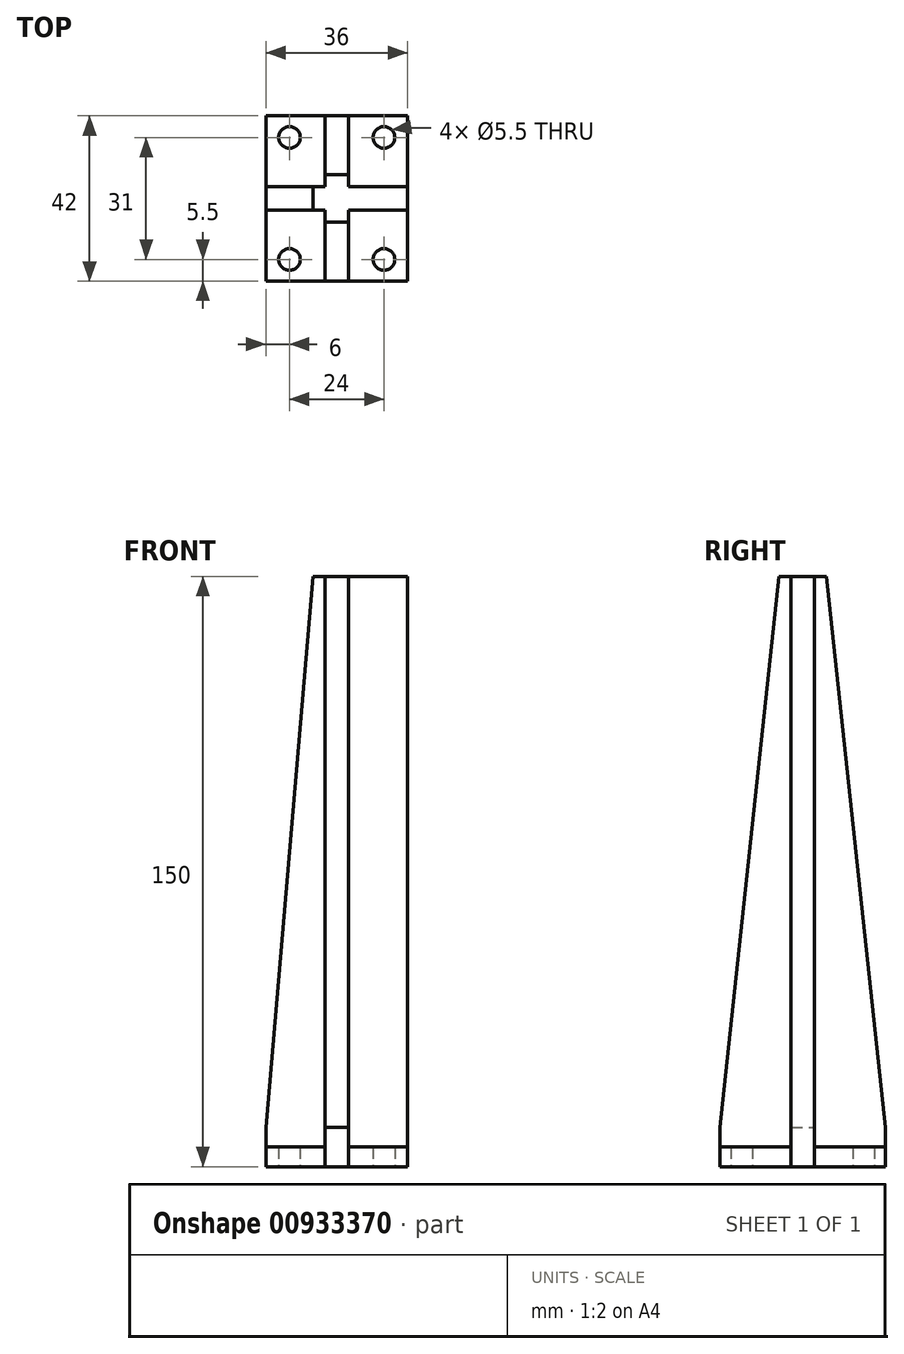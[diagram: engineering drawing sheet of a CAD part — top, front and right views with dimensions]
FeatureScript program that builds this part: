
annotation { "Feature Type Name" : "Feature", "Feature Type Description" : "" }
export const myFeature = defineFeature(function(context is Context, id is Id, definition is map)
    precondition{}
    {
        {
            var Q0;
            Q0=qCreatedBy(makeId("Top.planeOp"),FACE);
            var sketch = newSketch(context, id + "F0", { "sketchPlane" : qUnion([Q0])});
            skLineSegment(sketch, "E0.bottom", {"start": v(18, -21) * mm, "end": v(-18, -21) * mm});
            skLineSegment(sketch, "E0.top", {"start": v(18, 21) * mm, "end": v(-18, 21) * mm});
            skLineSegment(sketch, "E0.left", {"start": v(18, -21) * mm, "end": v(18, 21) * mm});
            skLineSegment(sketch, "E0.right", {"start": v(-18, -21) * mm, "end": v(-18, 21) * mm});
            skPoint(sketch, "E0.middle", {"position": v(0, 0) * mm});
            skCircle(sketch, "E1", {"center": v(-12, 15.5) * mm, "radius": 2.75 * mm});
            skCircle(sketch, "E2", {"center": v(12, 15.5) * mm, "radius": 2.75 * mm});
            skCircle(sketch, "E3", {"center": v(12, -15.5) * mm, "radius": 2.75 * mm});
            skCircle(sketch, "E4", {"center": v(-12, -15.5) * mm, "radius": 2.75 * mm});
            skLineSegment(sketch, "E5.bottom", {"start": v(3, -21) * mm, "end": v(-3, -21) * mm});
            skLineSegment(sketch, "E5.top", {"start": v(3, 21) * mm, "end": v(-3, 21) * mm});
            skLineSegment(sketch, "E5.left", {"start": v(3, -21) * mm, "end": v(3, 21) * mm});
            skLineSegment(sketch, "E5.right", {"start": v(-3, -21) * mm, "end": v(-3, 21) * mm});
            skLineSegment(sketch, "E6.bottom", {"start": v(-18, -3) * mm, "end": v(18, -3) * mm});
            skLineSegment(sketch, "E6.top", {"start": v(-18, 3) * mm, "end": v(18, 3) * mm});
            skLineSegment(sketch, "E6.left", {"start": v(-18, -3) * mm, "end": v(-18, 3) * mm});
            skLineSegment(sketch, "E6.right", {"start": v(18, -3) * mm, "end": v(18, 3) * mm});
            skSolve(sketch);
        }
        {
            var Q0;
            Q0=makeQuery(id+"F0.imprint","IMPRINT",FACE,{"disambiguationData":[TD([[makeQuery(id+"F0.imprint","IMPRINT",EDGE,{"derivedFrom":sQuery(id+"F0.wireOp",EDGE,"E2")}),-1.0]])]});
            var Q1;
            Q1=makeQuery(id+"F0.imprint","IMPRINT",FACE,{"disambiguationData":[TD([[makeQuery(id+"F0.imprint","IMPRINT",EDGE,{"derivedFrom":sQuery(id+"F0.wireOp",EDGE,"E1")}),-1.0]])]});
            var Q2;
            Q2=makeQuery(id+"F0.imprint","IMPRINT",FACE,{"disambiguationData":[TD([[makeQuery(id+"F0.imprint","IMPRINT",EDGE,{"derivedFrom":sQuery(id+"F0.wireOp",EDGE,"E4")}),-1.0]])]});
            var Q3;
            Q3=makeQuery(id+"F0.imprint","IMPRINT",FACE,{"disambiguationData":[TD([[makeQuery(id+"F0.imprint","IMPRINT",EDGE,{"derivedFrom":sQuery(id+"F0.wireOp",EDGE,"E3")}),-1.0]])]});
            extrude(context, id + "F1", {"entities" : qUnion([Q0, Q1, Q2, Q3]), "depth" : 5 * mm, "offsetDistance" : 25 * mm});
        }
        {
            var Q0;
            {var subQ0=sQuery(id+"F0.wireOp",EDGE,"E5.right");var subQ1=sQuery(id+"F0.wireOp",EDGE,"E0.top");var subQ2=makeQuery(id+"F0.imprint","INTERSECT",VERTEX,{"derivedFrom":[subQ1,subQ0]});Q0=makeQuery(id+"F0.imprint","IMPRINT",FACE,{"disambiguationData":[TD([[makeQuery(id+"F0.imprint","IMPRINT",EDGE,{"disambiguationData":[TD([[subQ2,1.0]])],"derivedFrom":subQ1}),1.0]])]});}
            var Q1;
            {var subQ0=sQuery(id+"F0.wireOp",EDGE,"E5.right");var subQ1=sQuery(id+"F0.wireOp",EDGE,"E0.bottom");var subQ2=makeQuery(id+"F0.imprint","INTERSECT",VERTEX,{"derivedFrom":[subQ1,subQ0]});Q1=makeQuery(id+"F0.imprint","IMPRINT",FACE,{"disambiguationData":[TD([[makeQuery(id+"F0.imprint","IMPRINT",EDGE,{"disambiguationData":[TD([[subQ2,1.0]])],"derivedFrom":subQ1}),-1.0]])]});}
            var Q2;
            {var subQ0=sQuery(id+"F0.wireOp",EDGE,"E6.top");var subQ1=sQuery(id+"F0.wireOp",EDGE,"E0.left");var subQ2=makeQuery(id+"F0.imprint","INTERSECT",VERTEX,{"derivedFrom":[subQ1,subQ0]});Q2=makeQuery(id+"F0.imprint","IMPRINT",FACE,{"disambiguationData":[TD([[makeQuery(id+"F0.imprint","IMPRINT",EDGE,{"disambiguationData":[TD([[subQ2,1.0]])],"derivedFrom":subQ1}),1.0]])]});}
            var Q3;
            {var subQ0=sQuery(id+"F0.wireOp",EDGE,"E6.top");var subQ1=sQuery(id+"F0.wireOp",EDGE,"E0.right");var subQ2=makeQuery(id+"F0.imprint","INTERSECT",VERTEX,{"derivedFrom":[subQ1,subQ0]});Q3=makeQuery(id+"F0.imprint","IMPRINT",FACE,{"disambiguationData":[TD([[makeQuery(id+"F0.imprint","IMPRINT",EDGE,{"disambiguationData":[TD([[subQ2,1.0]])],"derivedFrom":subQ1}),-1.0]])]});}
            var Q4;
            {var subQ0=sQuery(id+"F0.wireOp",EDGE,"E6.top");var subQ1=sQuery(id+"F0.wireOp",EDGE,"E5.left");var subQ2=makeQuery(id+"F0.imprint","INTERSECT",VERTEX,{"derivedFrom":[subQ1,subQ0]});Q4=makeQuery(id+"F0.imprint","IMPRINT",FACE,{"disambiguationData":[TD([[makeQuery(id+"F0.imprint","IMPRINT",EDGE,{"disambiguationData":[TD([[subQ2,1.0]])],"derivedFrom":subQ1}),1.0]])]});}
            extrude(context, id + "F2", {"entities" : qUnion([Q0, Q1, Q2, Q3, Q4]), "depth" : 150 * mm, "offsetDistance" : 25 * mm});
        }
        {
            var Q0;
            Q0=makeQuery(id+"F2.opExtrude","CAP_EDGE",EDGE,{"disambiguationData":[OSD([sQuery(id+"F0.wireOp",EDGE,"E0.top")])],"isStart":false});
            chamfer(context, id + "F3", {"entities" : qUnion([Q0]), "chamferType" : ChamferType.TWO_OFFSETS, "width1" : 15 * mm, "oppositeDirection" : false, "width2" : 140 * mm, "tangentPropagation" : true});
        }
        {
            var Q0;
            Q0=makeQuery(id+"F2.opExtrude","CAP_EDGE",EDGE,{"disambiguationData":[OSD([sQuery(id+"F0.wireOp",EDGE,"E0.bottom")])],"isStart":false});
            chamfer(context, id + "F4", {"entities" : qUnion([Q0]), "chamferType" : ChamferType.TWO_OFFSETS, "width1" : 140 * mm, "oppositeDirection" : false, "width2" : 15 * mm, "tangentPropagation" : true});
        }
        {
            var Q0;
            Q0=makeQuery(id+"F2.opExtrude","CAP_EDGE",EDGE,{"disambiguationData":[OSD([sQuery(id+"F0.wireOp",EDGE,"E0.right")])],"isStart":false});
            chamfer(context, id + "F5", {"entities" : qUnion([Q0]), "chamferType" : ChamferType.TWO_OFFSETS, "width1" : 140 * mm, "oppositeDirection" : false, "width2" : 12 * mm, "tangentPropagation" : true});
        }
    });
